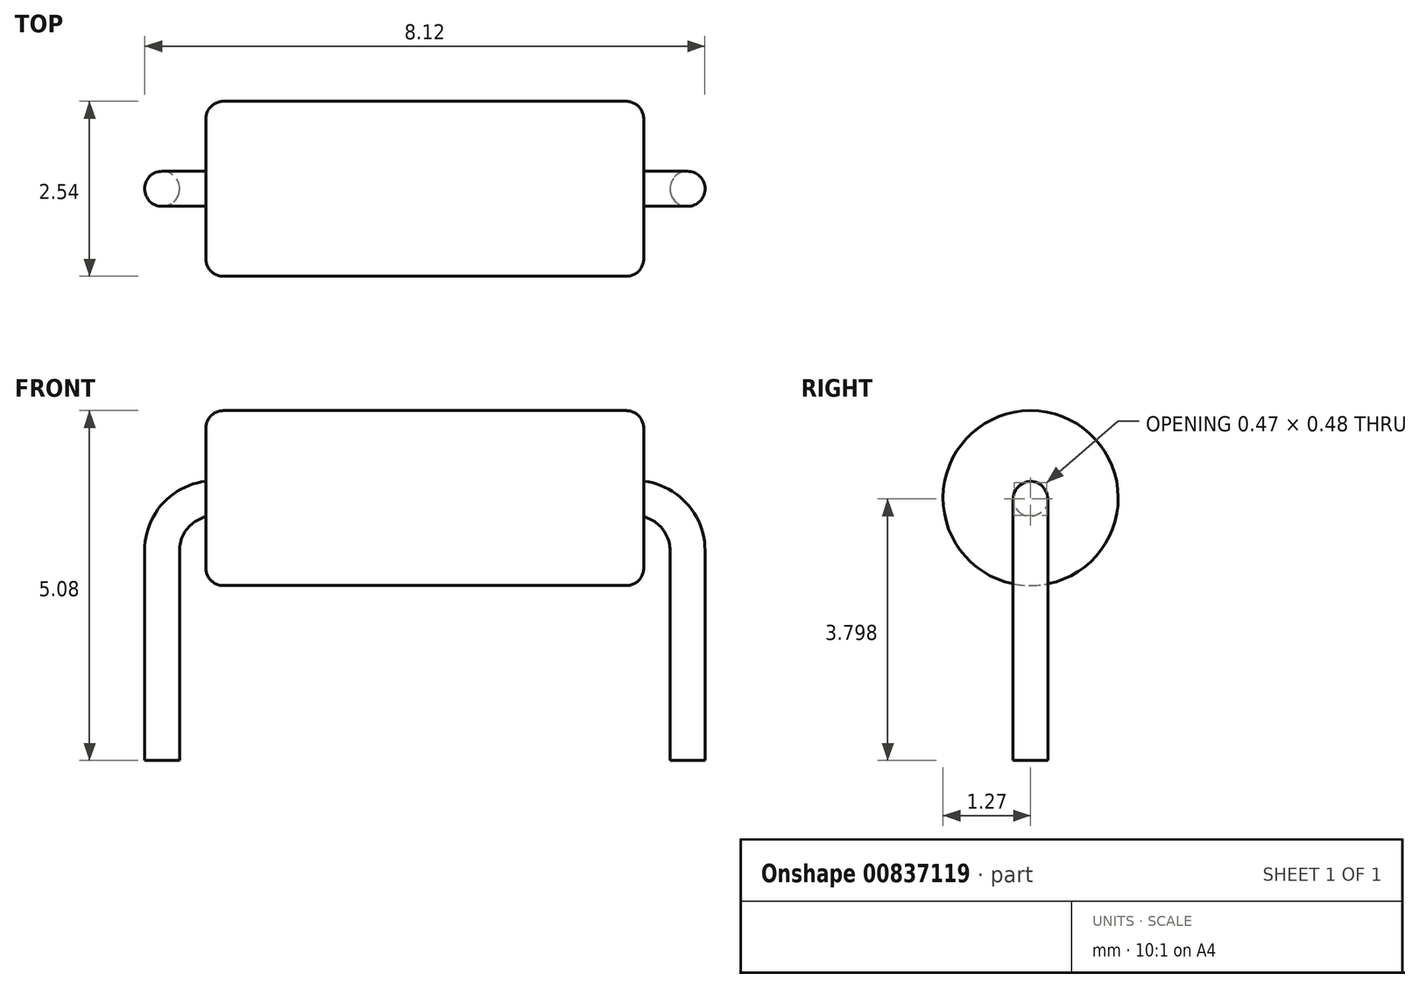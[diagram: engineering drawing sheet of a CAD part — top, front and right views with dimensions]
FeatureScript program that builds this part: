
annotation { "Feature Type Name" : "Feature", "Feature Type Description" : "" }
export const myFeature = defineFeature(function(context is Context, id is Id, definition is map)
    precondition{}
    {
        {
            var Q0;
            Q0=qCreatedBy(makeId("Front.planeOp"),FACE);
            var sketch = newSketch(context, id + "F0", { "sketchPlane" : qUnion([Q0])});
            skLineSegment(sketch, "E0.bottom", {"start": v(-3.18, 0) * mm, "end": v(3.18, 0) * mm});
            skLineSegment(sketch, "E0.left", {"start": v(-3.18, 0) * mm, "end": v(-3.18, 1.27) * mm});
            skLineSegment(sketch, "E0.right", {"start": v(3.18, 0) * mm, "end": v(3.18, 1.27) * mm});
            skLineSegment(sketch, "E1.trimOffspring", {"start": v(-3.17, 1.27) * mm, "end": v(3.17, 1.27) * mm});
            skSolve(sketch);
        }
        {
            var Q0;
            Q0=qSketchRegion(id+"F0",true);
            var Q1;
            Q1=sQuery(id+"F0.wireOp",EDGE,"E0.bottom");
            revolve(context, id + "F1", {"surfaceOperationType" : NewSurfaceOperationType.NEW, "entities" : qUnion([Q0]), "axis" : qUnion([Q1]), "revolveType" : RevolveType.FULL});
        }
        {
            var Q0;
            Q0=makeQuery(id+"F1.opRevolve","SWEPT_EDGE",EDGE,{"disambiguationData":[OSD([sQuery(id+"F0.wireOp",EDGE,"E0.right"),sQuery(id+"F0.wireOp",EDGE,"E1.trimOffspring")])]});
            var Q1;
            Q1=makeQuery(id+"F1.opRevolve","SWEPT_EDGE",EDGE,{"disambiguationData":[OSD([sQuery(id+"F0.wireOp",EDGE,"E0.top"),sQuery(id+"F0.wireOp",EDGE,"E0.left")])]});
            fillet(context, id + "F2", {"entities" : qUnion([Q0, Q1]), "radius" : 0.25 * mm, "tangentPropagation" : true, "allowEdgeOverflow" : false});
        }
        {
            var Q0;
            Q0=qCreatedBy(makeId("Front.planeOp"),FACE);
            var sketch = newSketch(context, id + "F3", { "sketchPlane" : qUnion([Q0])});
            skLineSegment(sketch, "E2", {"start": v(-3.05, 0) * mm, "end": v(3.05, 0) * mm});
            skLineSegment(sketch, "E3", {"start": v(3.81, -0.76) * mm, "end": v(3.81, -3.81) * mm});
            skLineSegment(sketch, "E4", {"start": v(-3.81, -0.76) * mm, "end": v(-3.81, -3.81) * mm});
            skLineSegment(sketch, "E5", {"start": v(-3.81, -3.81) * mm, "end": v(3.81, -3.81) * mm, "construction": true});
            skPoint(sketch, "E6.visualSharp", {"position": v(-3.81, 0) * mm});
            skArc(sketch, "E6.filletArc", {"start": v(-3.05, 0) * mm, "mid": v(-3.59, -0.22) * mm, "end": v(-3.81, -0.76) * mm});
            skPoint(sketch, "E7.visualSharp", {"position": v(3.81, 0) * mm});
            skArc(sketch, "E7.filletArc", {"start": v(3.81, -0.76) * mm, "mid": v(3.59, -0.22) * mm, "end": v(3.05, 0) * mm});
            skSolve(sketch);
        }
        {
            var Q0;
            Q0=qCreatedBy(makeId("Top.planeOp"),FACE);
            cPlane(context, id + "F4", {"entities" : qUnion([Q0]), "cplaneType" : CPlaneType.OFFSET, "offset" : 3.8 * mm, "oppositeDirection" : true, "width" : 152.4 * mm, "height" : 152.4 * mm});
        }
        {
            var Q0;
            Q0=qCreatedBy(id+"F4.planeOp",FACE);
            var sketch = newSketch(context, id + "F5", { "sketchPlane" : qUnion([Q0])});
            skCircle(sketch, "E8", {"center": v(-3.81, 0) * mm, "radius": 0.25 * mm});
            skSolve(sketch);
        }
        {
            var Q0;
            Q0=makeQuery(id+"F5.imprint","IMPRINT",FACE,{"disambiguationData":[TD([[makeQuery(id+"F5.imprint","IMPRINT",EDGE,{"derivedFrom":sQuery(id+"F5.wireOp",EDGE,"E8")}),1.0]])]});
            var Q1;
            Q1=sQuery(id+"F3.wireOp",EDGE,"E4");
            var Q2;
            Q2=sQuery(id+"F3.wireOp",EDGE,"E6.filletArc");
            var Q3;
            Q3=sQuery(id+"F3.wireOp",EDGE,"E2");
            var Q4;
            Q4=sQuery(id+"F3.wireOp",EDGE,"E7.filletArc");
            var Q5;
            Q5=sQuery(id+"F3.wireOp",EDGE,"E3");
            sweep(context, id + "F6", {"operationType" : NewBodyOperationType.ADD, "profiles" : qUnion([Q0]), "path" : qUnion([Q1, Q2, Q3, Q4, Q5])});
        }
    });
